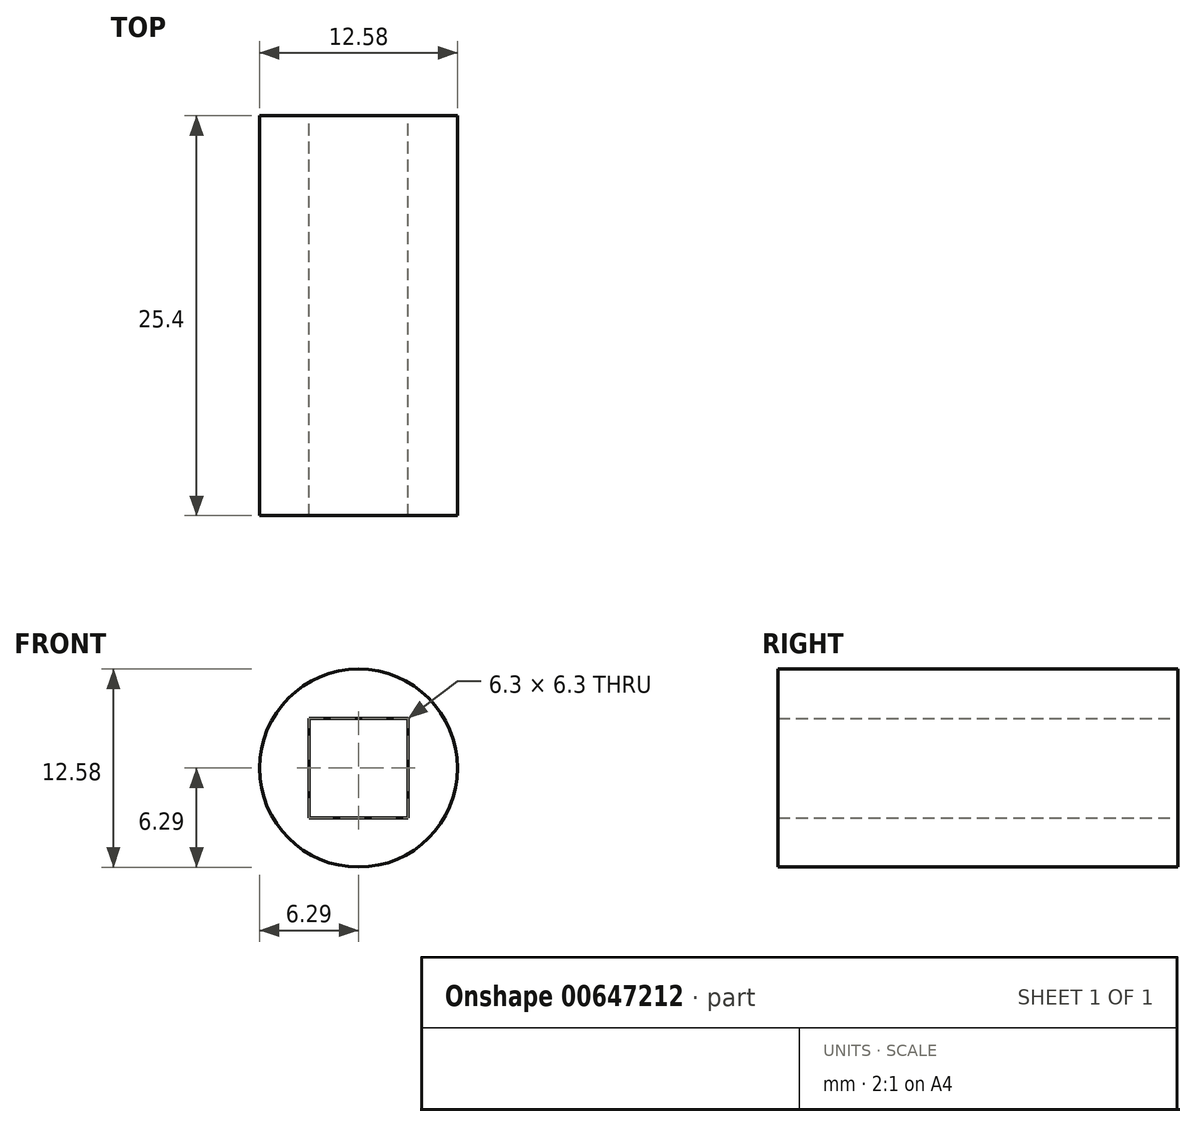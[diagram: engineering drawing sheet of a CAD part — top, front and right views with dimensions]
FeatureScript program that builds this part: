
annotation { "Feature Type Name" : "Feature", "Feature Type Description" : "" }
export const myFeature = defineFeature(function(context is Context, id is Id, definition is map)
    precondition{}
    {
        {
            var Q0;
            Q0=qCreatedBy(makeId("Front.planeOp"),FACE);
            var sketch = newSketch(context, id + "F0", { "sketchPlane" : qUnion([Q0])});
            skLineSegment(sketch, "E0.bottom", {"start": v(-3.15, 3.15) * mm, "end": v(3.15, 3.15) * mm});
            skLineSegment(sketch, "E0.top", {"start": v(-3.15, -3.15) * mm, "end": v(3.15, -3.15) * mm});
            skLineSegment(sketch, "E0.left", {"start": v(-3.15, 3.15) * mm, "end": v(-3.15, -3.15) * mm});
            skLineSegment(sketch, "E0.right", {"start": v(3.15, 3.15) * mm, "end": v(3.15, -3.15) * mm});
            skCircle(sketch, "E1", {"center": v(0, 0) * mm, "radius": 6.29 * mm});
            skSolve(sketch);
        }
        {
            var Q0;
            Q0=makeQuery(id+"F0.imprint","IMPRINT",FACE,{"disambiguationData":[TD([[makeQuery(id+"F0.imprint","IMPRINT",EDGE,{"derivedFrom":sQuery(id+"F0.wireOp",EDGE,"E0.bottom")}),1.0]])]});
            extrude(context, id + "F1", {"entities" : qUnion([Q0]), "depth" : 25.4 * mm, "offsetDistance" : 25.4 * mm});
        }
    });
